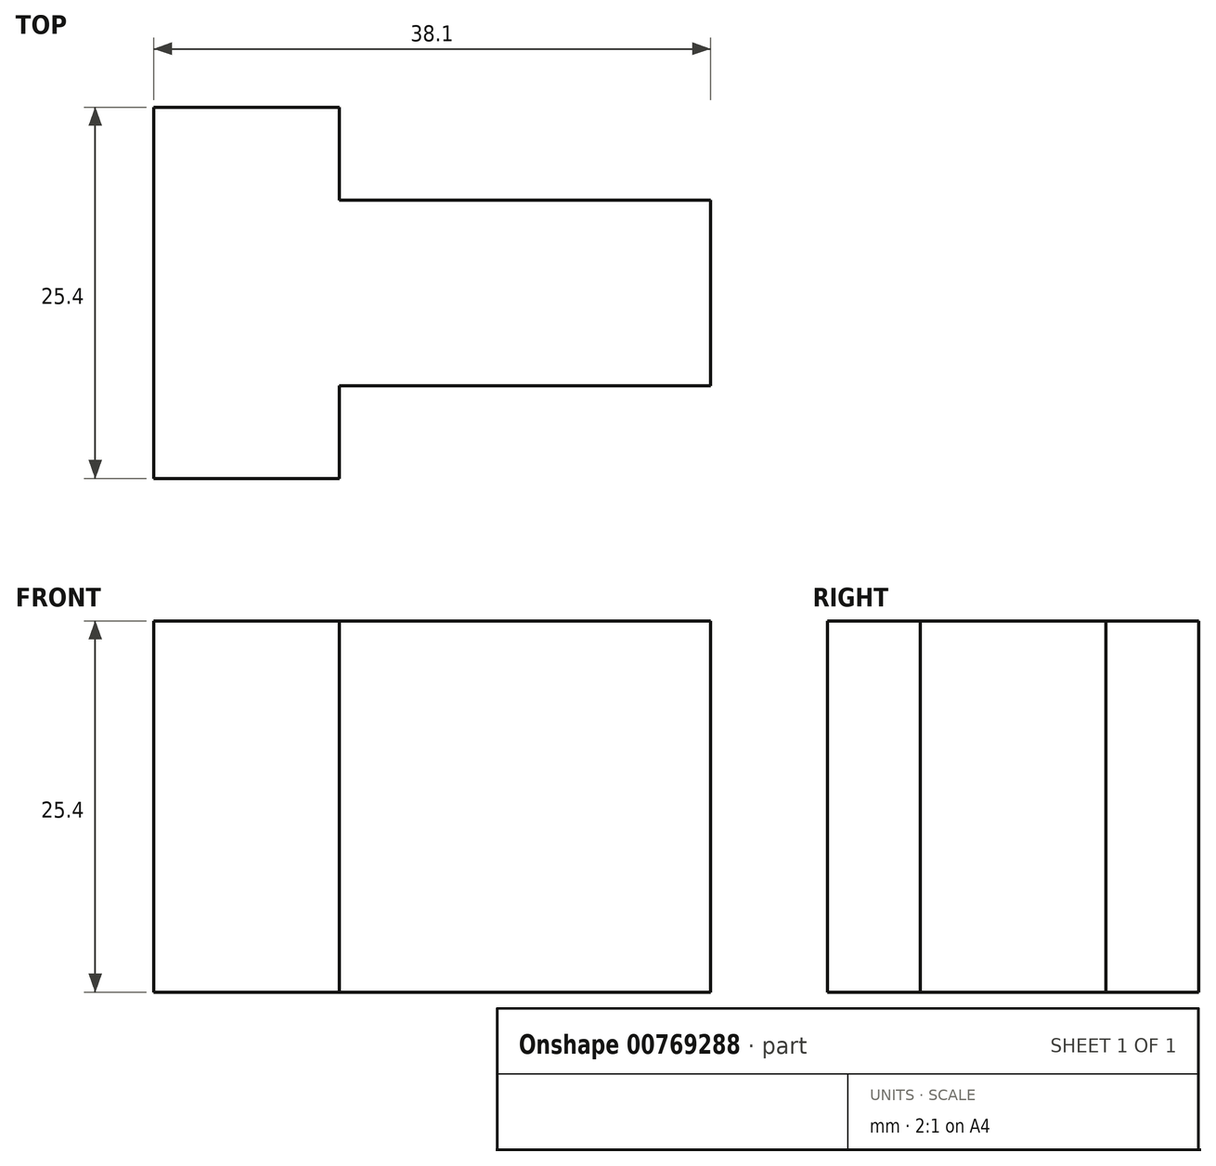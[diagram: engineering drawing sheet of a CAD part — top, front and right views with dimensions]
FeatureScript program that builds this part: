
annotation { "Feature Type Name" : "Feature", "Feature Type Description" : "" }
export const myFeature = defineFeature(function(context is Context, id is Id, definition is map)
    precondition{}
    {
        {
            var Q0;
            Q0=qCreatedBy(makeId("Top.planeOp"),FACE);
            var sketch = newSketch(context, id + "F0", { "sketchPlane" : qUnion([Q0])});
            skLineSegment(sketch, "E0", {"start": v(0, 0) * mm, "end": v(0, -25.4) * mm});
            skLineSegment(sketch, "E1", {"start": v(0, -25.4) * mm, "end": v(12.7, -25.4) * mm});
            skLineSegment(sketch, "E2", {"start": v(12.7, -25.4) * mm, "end": v(12.7, -19.05) * mm});
            skLineSegment(sketch, "E3", {"start": v(12.7, -19.05) * mm, "end": v(38.1, -19.05) * mm});
            skLineSegment(sketch, "E4", {"start": v(38.1, -19.05) * mm, "end": v(38.1, -6.35) * mm});
            skLineSegment(sketch, "E5", {"start": v(38.1, -6.35) * mm, "end": v(12.7, -6.35) * mm});
            skLineSegment(sketch, "E6", {"start": v(12.7, -6.35) * mm, "end": v(12.7, 0) * mm});
            skLineSegment(sketch, "E7", {"start": v(12.7, 0) * mm, "end": v(0, 0) * mm});
            skSolve(sketch);
        }
        {
            var Q0;
            Q0=makeQuery(id+"F0.imprint","IMPRINT",FACE,{"disambiguationData":[TD([[makeQuery(id+"F0.imprint","IMPRINT",EDGE,{"derivedFrom":sQuery(id+"F0.wireOp",EDGE,"E0")}),1.0]])]});
            extrude(context, id + "F1", {"entities" : qUnion([Q0]), "depth" : 25.4 * mm, "offsetDistance" : 25.4 * mm});
        }
    });
